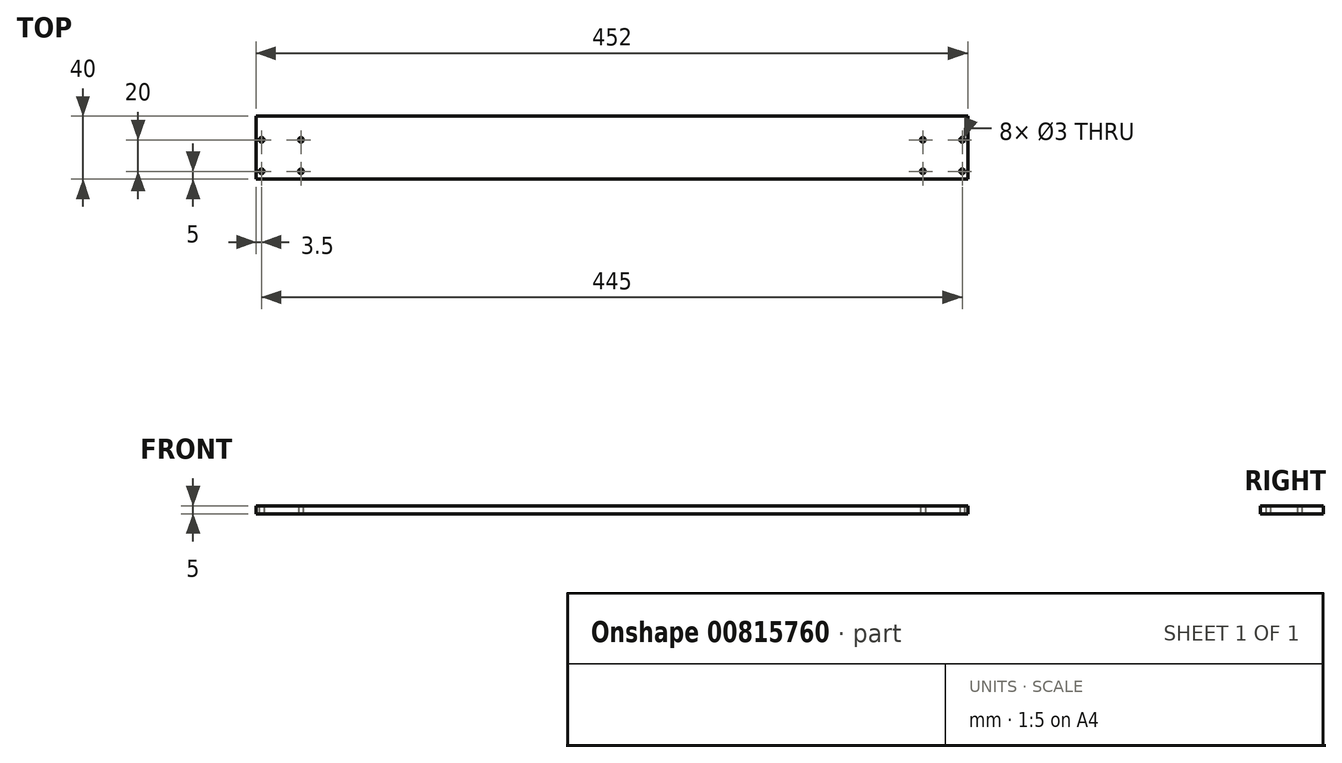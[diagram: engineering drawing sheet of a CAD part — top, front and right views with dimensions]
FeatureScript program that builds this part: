
annotation { "Feature Type Name" : "Feature", "Feature Type Description" : "" }
export const myFeature = defineFeature(function(context is Context, id is Id, definition is map)
    precondition{}
    {
        {
            var Q0;
            Q0=qCreatedBy(makeId("Top.planeOp"),FACE);
            var sketch = newSketch(context, id + "F0", { "sketchPlane" : qUnion([Q0])});
            skLineSegment(sketch, "E0.left", {"start": v(197.5, 0) * mm, "end": v(197.5, 0) * mm});
            skLineSegment(sketch, "E0.right", {"start": v(-197.5, 0) * mm, "end": v(-197.5, 0) * mm});
            skLineSegment(sketch, "E1.bottom", {"start": v(226, -5) * mm, "end": v(-226, -5) * mm});
            skLineSegment(sketch, "E1.top", {"start": v(226, 35) * mm, "end": v(-226, 35) * mm});
            skLineSegment(sketch, "E1.left", {"start": v(226, -5) * mm, "end": v(226, 35) * mm});
            skLineSegment(sketch, "E1.right", {"start": v(-226, -5) * mm, "end": v(-226, 35) * mm});
            skPoint(sketch, "E1.middle", {"position": v(0, 0) * mm});
            skPoint(sketch, "E2", {"position": v(-222.5, 0) * mm});
            skPoint(sketch, "E3", {"position": v(222.5, 0) * mm});
            skPoint(sketch, "E4", {"position": v(-197.5, 0) * mm});
            skPoint(sketch, "E5", {"position": v(197.5, 0) * mm});
            skLineSegment(sketch, "E6.bottom", {"start": v(197.5, 0) * mm, "end": v(222.5, 0) * mm});
            skLineSegment(sketch, "E6.top", {"start": v(197.5, 20) * mm, "end": v(222.5, 20) * mm});
            skLineSegment(sketch, "E6.left", {"start": v(197.5, 0) * mm, "end": v(197.5, 20) * mm});
            skLineSegment(sketch, "E6.right", {"start": v(222.5, 0) * mm, "end": v(222.5, 20) * mm});
            skPoint(sketch, "E7", {"position": v(197.5, 20) * mm});
            skPoint(sketch, "E8", {"position": v(222.5, 20) * mm});
            skLineSegment(sketch, "E9.bottom", {"start": v(-222.5, 0) * mm, "end": v(-197.5, 0) * mm});
            skLineSegment(sketch, "E9.top", {"start": v(-222.5, 20) * mm, "end": v(-197.5, 20) * mm});
            skLineSegment(sketch, "E9.left", {"start": v(-222.5, 0) * mm, "end": v(-222.5, 20) * mm});
            skLineSegment(sketch, "E9.right", {"start": v(-197.5, 0) * mm, "end": v(-197.5, 20) * mm});
            skPoint(sketch, "E10", {"position": v(-222.5, 20) * mm});
            skPoint(sketch, "E11", {"position": v(-197.5, 20) * mm});
            skSolve(sketch);
        }
        {
            var Q0;
            Q0=makeQuery(id+"F0.imprint","IMPRINT",FACE,{"disambiguationData":[TD([[makeQuery(id+"F0.imprint","IMPRINT",EDGE,{"derivedFrom":sQuery(id+"F0.wireOp",EDGE,"E1.bottom")}),-1.0]])]});
            var Q1;
            Q1=makeQuery(id+"F0.imprint","IMPRINT",FACE,{"disambiguationData":[TD([[makeQuery(id+"F0.imprint","IMPRINT",EDGE,{"derivedFrom":sQuery(id+"F0.wireOp",EDGE,"1djjfet9-r8II-OvUN-IzRK-AluCdZYkfCC9.bottom")}),-1.0]])]});
            var Q2;
            Q2=makeQuery(id+"F0.imprint","IMPRINT",FACE,{"disambiguationData":[TD([[makeQuery(id+"F0.imprint","IMPRINT",EDGE,{"derivedFrom":sQuery(id+"F0.wireOp",EDGE,"wCtzki7v-z0jc-xLA0-qSaf-msJyXheFnKOS.bottom")}),1.0]])]});
            var Q3;
            Q3=makeQuery(id+"F0.imprint","IMPRINT",FACE,{"disambiguationData":[TD([[makeQuery(id+"F0.imprint","IMPRINT",EDGE,{"derivedFrom":sQuery(id+"F0.wireOp",EDGE,"C0Bq9qiu-bVQi-CqkN-PGBD-0bIsM2nWbNyo.bottom")}),1.0]])]});
            var Q4;
            Q4=makeQuery(id+"F0.imprint","IMPRINT",FACE,{"disambiguationData":[TD([[makeQuery(id+"F0.imprint","IMPRINT",EDGE,{"derivedFrom":sQuery(id+"F0.wireOp",EDGE,"E6.bottom")}),1.0]])]});
            var Q5;
            Q5=makeQuery(id+"F0.imprint","IMPRINT",FACE,{"disambiguationData":[TD([[makeQuery(id+"F0.imprint","IMPRINT",EDGE,{"derivedFrom":sQuery(id+"F0.wireOp",EDGE,"E9.bottom")}),1.0]])]});
            extrude(context, id + "F1", {"entities" : qUnion([Q0, Q1, Q2, Q3, Q4, Q5]), "depth" : 5 * mm, "offsetDistance" : 25 * mm});
        }
        {
            var Q0;
            Q0=sQuery(id+"F0.wireOp",VERTEX,"E2");
            var Q1;
            Q1=sQuery(id+"F0.wireOp",VERTEX,"E4");
            var Q2;
            Q2=sQuery(id+"F0.wireOp",VERTEX,"E5");
            var Q3;
            Q3=sQuery(id+"F0.wireOp",VERTEX,"E3");
            var Q4;
            Q4=sQuery(id+"F0.wireOp",VERTEX,"1djjfet9-r8II-OvUN-IzRK-AluCdZYkfCC9.top.start");
            var Q5;
            Q5=sQuery(id+"F0.wireOp",VERTEX,"1djjfet9-r8II-OvUN-IzRK-AluCdZYkfCC9.top.end");
            var Q6;
            Q6=sQuery(id+"F0.wireOp",VERTEX,"12411fc7-a27c-42b5-9f3d-f57f29c69cfd");
            var Q7;
            Q7=sQuery(id+"F0.wireOp",VERTEX,"97257abe-7b92-4f64-87fc-5fa46ae78754");
            var Q8;
            Q8=sQuery(id+"F0.wireOp",VERTEX,"635f9920-3bd8-4998-b842-c92dc46858d5");
            var Q9;
            Q9=sQuery(id+"F0.wireOp",VERTEX,"c6f7a53d-bc70-49f4-b5e3-357c453e1794");
            var Q10;
            Q10=sQuery(id+"F0.wireOp",VERTEX,"ae7f2b9b-8ab5-4040-81d6-3f2d54d9ca8f");
            var Q11;
            Q11=sQuery(id+"F0.wireOp",VERTEX,"829b7a19-1b9d-4150-989c-15a8ebfd1b0a");
            var Q12;
            Q12=sQuery(id+"F0.wireOp",VERTEX,"E10");
            var Q13;
            Q13=sQuery(id+"F0.wireOp",VERTEX,"E11");
            var Q14;
            Q14=sQuery(id+"F0.wireOp",VERTEX,"E8");
            var Q15;
            Q15=sQuery(id+"F0.wireOp",VERTEX,"E7");
            var Q16;
            Q16=makeQuery(id+"F1.opExtrude","SWEPT_BODY",BODY,{"disambiguationData":[OSD([sQuery(id+"F0.wireOp",EDGE,"E1.bottom"),sQuery(id+"F0.wireOp",EDGE,"E1.top"),sQuery(id+"F0.wireOp",EDGE,"E1.left"),sQuery(id+"F0.wireOp",EDGE,"E1.right")])]});
            hole(context, id + "F2", {"style" : HoleStyle.SIMPLE, "endStyle" : HoleEndStyle.THROUGH, "oppositeDirection" : true, "holeDiameter" : 3 * mm, "majorDiameter" : 5 * mm, "isTappedThrough" : true, "tappedDepth" : 12 * mm, "tapClearance" : 3, "locations" : qUnion([Q0, Q1, Q2, Q3, Q4, Q5, Q6, Q7, Q8, Q9, Q10, Q11, Q12, Q13, Q14, Q15]), "scope" : qUnion([Q16])});
        }
    });
